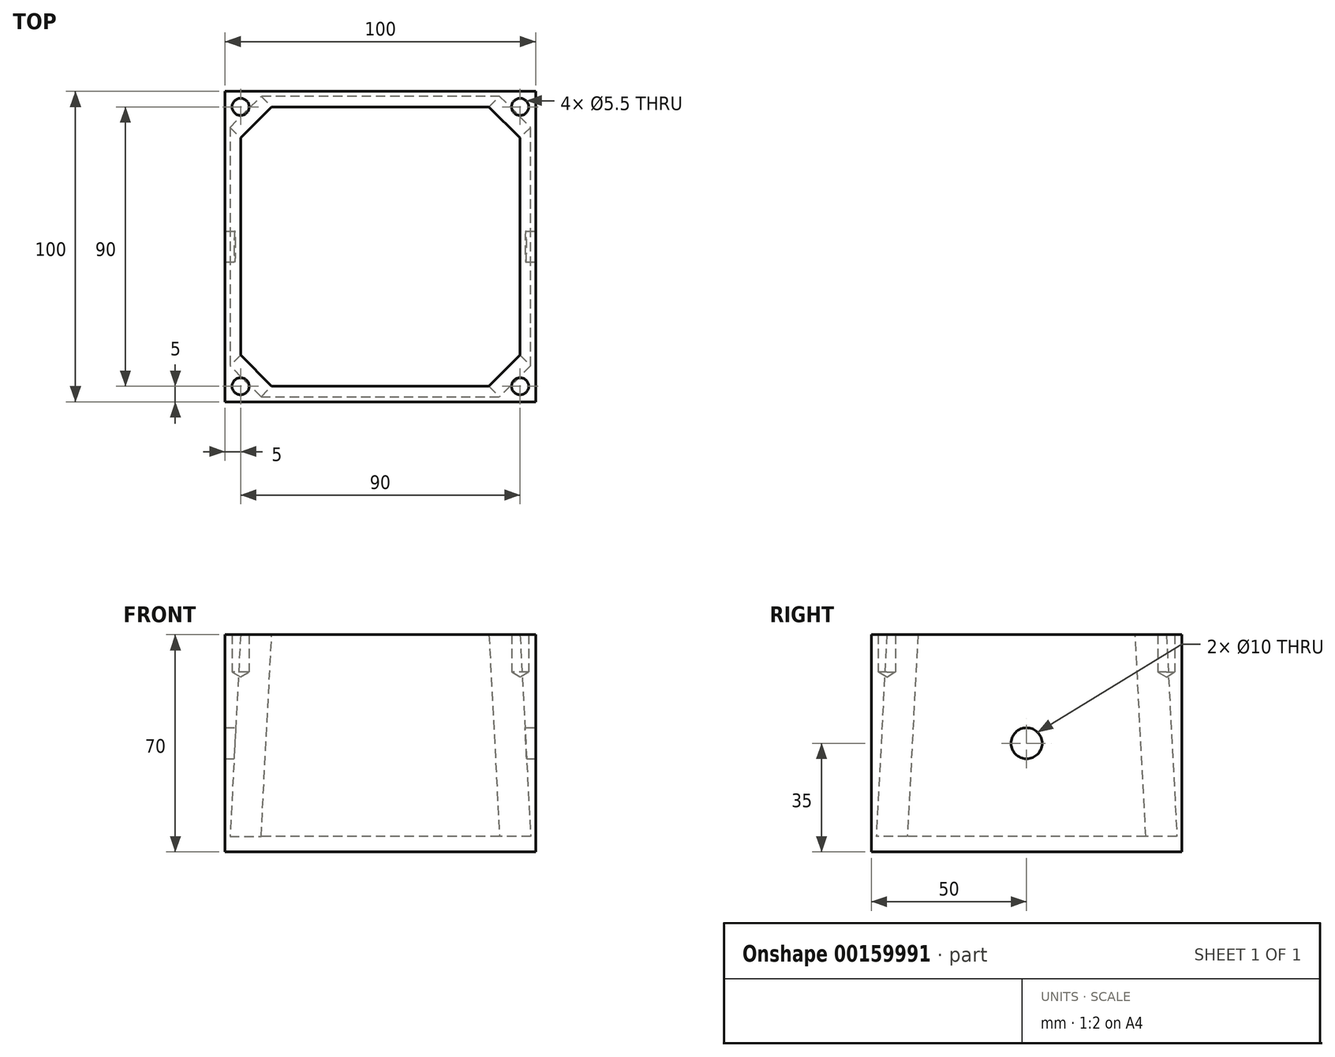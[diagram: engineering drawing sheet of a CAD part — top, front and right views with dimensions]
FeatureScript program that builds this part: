
annotation { "Feature Type Name" : "Feature", "Feature Type Description" : "" }
export const myFeature = defineFeature(function(context is Context, id is Id, definition is map)
    precondition{}
    {
        {
            var Q0;
            Q0=qCreatedBy(makeId("Top.planeOp"),FACE);
            var sketch = newSketch(context, id + "F0", { "sketchPlane" : qUnion([Q0])});
            skLineSegment(sketch, "E0.bottom", {"start": v(-50, 50) * mm, "end": v(50, 50) * mm});
            skLineSegment(sketch, "E0.top", {"start": v(-50, -50) * mm, "end": v(50, -50) * mm});
            skLineSegment(sketch, "E0.left", {"start": v(-50, 50) * mm, "end": v(-50, -50) * mm});
            skLineSegment(sketch, "E0.right", {"start": v(50, 50) * mm, "end": v(50, -50) * mm});
            skPoint(sketch, "E0.middle", {"position": v(0, 0) * mm});
            skSolve(sketch);
        }
        {
            var Q0;
            Q0=makeQuery(id+"F0.imprint","IMPRINT",FACE,{"disambiguationData":[TD([[makeQuery(id+"F0.imprint","IMPRINT",EDGE,{"derivedFrom":sQuery(id+"F0.wireOp",EDGE,"E0.bottom")}),-1.0]])]});
            extrude(context, id + "F1", {"entities" : qUnion([Q0]), "depth" : 70 * mm});
        }
        {
            var Q0;
            Q0=makeQuery(id+"F1.opExtrude","CAP_FACE",FACE,{"disambiguationData":[OSD([sQuery(id+"F0.wireOp",EDGE,"E0.bottom"),sQuery(id+"F0.wireOp",EDGE,"E0.top"),sQuery(id+"F0.wireOp",EDGE,"E0.left"),sQuery(id+"F0.wireOp",EDGE,"E0.right")])],"isStart":false});
            var sketch = newSketch(context, id + "F2", { "sketchPlane" : qUnion([Q0])});
            skLineSegment(sketch, "E1.0", {"start": v(-45, 45) * mm, "end": v(45, 45) * mm});
            skLineSegment(sketch, "E1.1", {"start": v(-45, 45) * mm, "end": v(-45, -45) * mm});
            skLineSegment(sketch, "E1.2", {"start": v(-45, -45) * mm, "end": v(45, -45) * mm});
            skLineSegment(sketch, "E1.3", {"start": v(45, 45) * mm, "end": v(45, -45) * mm});
            skSolve(sketch);
        }
        {
            var Q0;
            Q0=makeQuery(id+"F2.imprint","IMPRINT",FACE,{"disambiguationData":[TD([[makeQuery(id+"F2.imprint","IMPRINT",EDGE,{"derivedFrom":sQuery(id+"F2.wireOp",EDGE,"E1.0")}),-1.0]])]});
            extrude(context, id + "F3", {"entities" : qUnion([Q0]), "operationType" : NewBodyOperationType.REMOVE, "oppositeDirection" : true, "depth" : 65 * mm, "hasDraft" : true, "draftAngle" : 3 * degree});
        }
        {
            var Q0;
            Q0=makeQuery(id+"F1.opExtrude","SWEPT_FACE",FACE,{"disambiguationData":[OSD([sQuery(id+"F0.wireOp",EDGE,"E0.right")])]});
            var sketch = newSketch(context, id + "F4", { "sketchPlane" : qUnion([Q0])});
            skCircle(sketch, "E2", {"center": v(0, 35) * mm, "radius": 5 * mm});
            skPoint(sketch, "E2.centerSnap0", {"position": v(-50, 35) * mm});
            skSolve(sketch);
        }
        {
            var Q0;
            Q0=makeQuery(id+"F4.imprint","IMPRINT",FACE,{"disambiguationData":[TD([[makeQuery(id+"F4.imprint","IMPRINT",EDGE,{"derivedFrom":sQuery(id+"F4.wireOp",EDGE,"E2")}),1.0]])]});
            var Q1;
            Q1=makeQuery(id+"F1.opExtrude","SWEPT_FACE",FACE,{"disambiguationData":[OSD([sQuery(id+"F0.wireOp",EDGE,"E0.left")])]});
            extrude(context, id + "F5", {"entities" : qUnion([Q0, Q1]), "operationType" : NewBodyOperationType.REMOVE, "endBound" : BoundingType.THROUGH_ALL, "oppositeDirection" : true, "depth" : 25 * mm});
        }
        {
            var Q0;
            Q0=makeQuery(id+"F3.boolean.opBoolean","COPY",EDGE,{"derivedFrom":makeQuery(id+"F3.opExtrude","SWEPT_EDGE",EDGE,{"disambiguationData":[OSD([sQuery(id+"F2.wireOp",EDGE,"E1.0"),sQuery(id+"F2.wireOp",EDGE,"E1.3")])]})});
            var Q1;
            Q1=makeQuery(id+"F3.boolean.opBoolean","COPY",EDGE,{"derivedFrom":makeQuery(id+"F3.opExtrude","SWEPT_EDGE",EDGE,{"disambiguationData":[OSD([sQuery(id+"F2.wireOp",EDGE,"E1.0"),sQuery(id+"F2.wireOp",EDGE,"E1.1")])]})});
            var Q2;
            Q2=makeQuery(id+"F3.boolean.opBoolean","COPY",EDGE,{"derivedFrom":makeQuery(id+"F3.opExtrude","SWEPT_EDGE",EDGE,{"disambiguationData":[OSD([sQuery(id+"F2.wireOp",EDGE,"E1.1"),sQuery(id+"F2.wireOp",EDGE,"E1.2")])]})});
            var Q3;
            Q3=makeQuery(id+"F3.boolean.opBoolean","COPY",EDGE,{"derivedFrom":makeQuery(id+"F3.opExtrude","SWEPT_EDGE",EDGE,{"disambiguationData":[OSD([sQuery(id+"F2.wireOp",EDGE,"E1.2"),sQuery(id+"F2.wireOp",EDGE,"E1.3")])]})});
            chamfer(context, id + "F6", {"entities" : qUnion([Q0, Q1, Q2, Q3]), "width" : 10 * mm, "tangentPropagation" : true});
        }
        {
            var Q0;
            Q0=sQuery(id+"F2.wireOp",VERTEX,"E1.2.start");
            var Q1;
            Q1=sQuery(id+"F2.wireOp",VERTEX,"E1.1.start");
            var Q2;
            Q2=sQuery(id+"F2.wireOp",VERTEX,"E1.3.start");
            var Q3;
            Q3=sQuery(id+"F2.wireOp",VERTEX,"E1.3.end");
            var Q4;
            Q4=makeQuery(id+"F1.opExtrude","SWEPT_BODY",BODY,{"disambiguationData":[OSD([sQuery(id+"F0.wireOp",EDGE,"E0.bottom"),sQuery(id+"F0.wireOp",EDGE,"E0.top"),sQuery(id+"F0.wireOp",EDGE,"E0.left"),sQuery(id+"F0.wireOp",EDGE,"E0.right")])]});
            hole(context, id + "F7", {"style" : HoleStyle.SIMPLE, "endStyle" : HoleEndStyle.BLIND, "standardTappedOrClearance" : lookupTablePath({ "standard" : "ISO", "fit" : "Normal", "size" : "M5", "type" : "Clearance" }), "standardBlindInLast" : lookupTablePath({ "fit" : "Standard", "standard" : "ISO", "size" : "M5", "type" : "Clearance" }), "holeDiameter" : 5.5 * mm, "holeDepth" : 12 * mm, "locations" : qUnion([Q0, Q1, Q2, Q3]), "scope" : qUnion([Q4]), "startStyle" : HoleStartStyle.PART});
        }
    });
